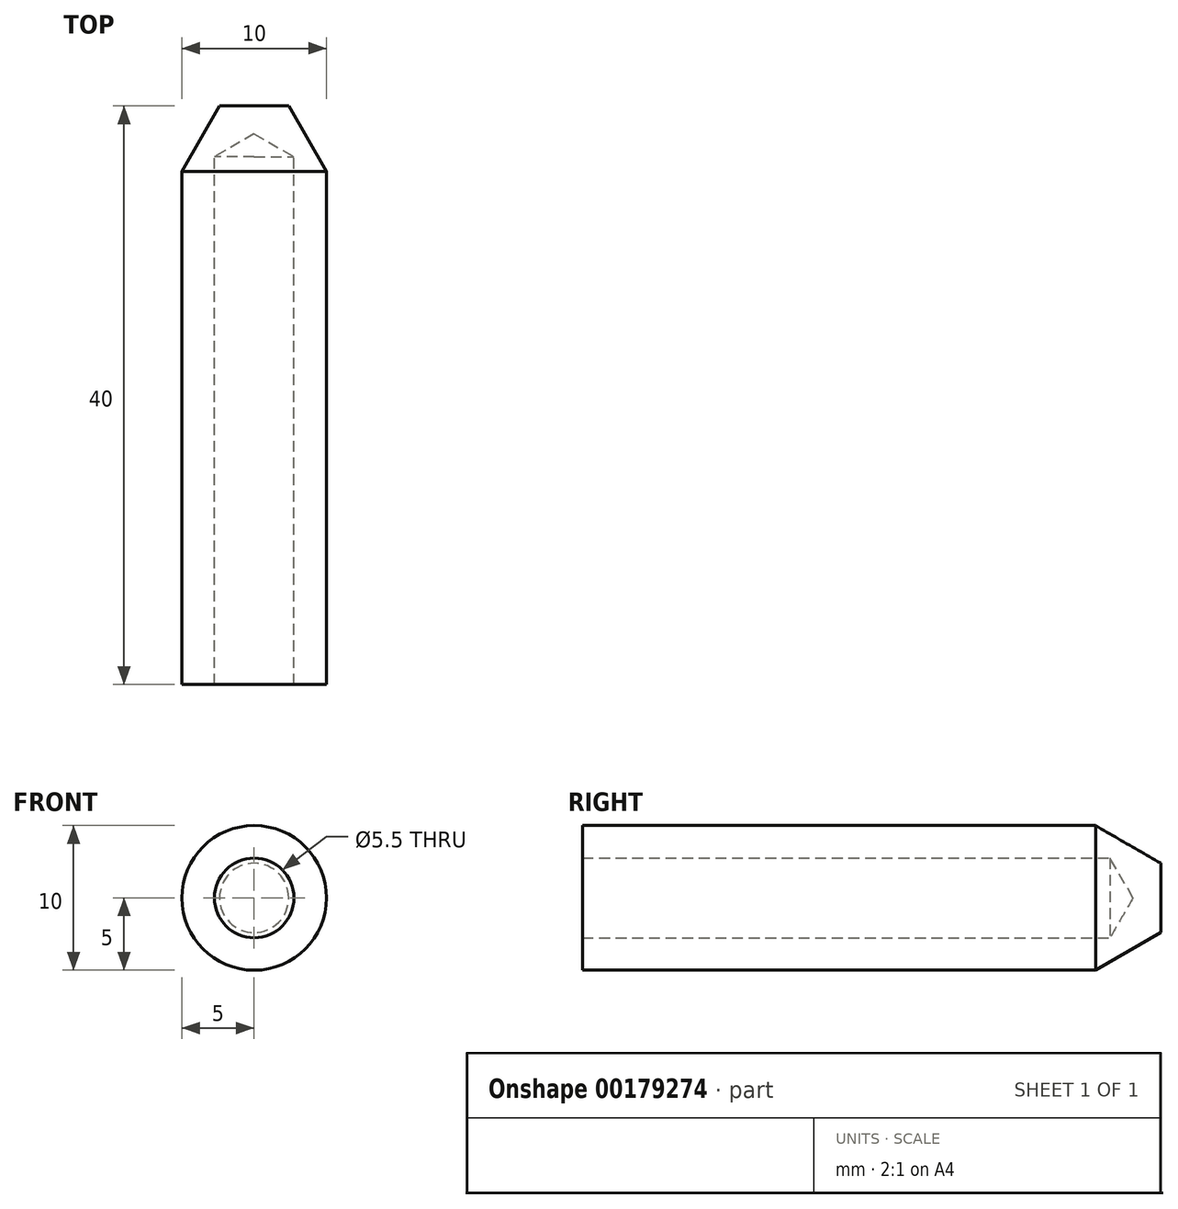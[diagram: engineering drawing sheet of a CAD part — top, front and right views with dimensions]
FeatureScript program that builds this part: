
annotation { "Feature Type Name" : "Feature", "Feature Type Description" : "" }
export const myFeature = defineFeature(function(context is Context, id is Id, definition is map)
    precondition{}
    {
        {
            var Q0;
            Q0=qCreatedBy(makeId("Right.planeOp"),FACE);
            var sketch = newSketch(context, id + "F0", { "sketchPlane" : qUnion([Q0])});
            skLineSegment(sketch, "E0", {"start": v(0, 5) * mm, "end": v(35.49, 5) * mm});
            skLineSegment(sketch, "E1", {"start": v(35.49, 5) * mm, "end": v(40, 2.4) * mm});
            skLineSegment(sketch, "E2", {"start": v(40, 2.4) * mm, "end": v(40, 0) * mm});
            skLineSegment(sketch, "E3", {"start": v(40, 0) * mm, "end": v(38.09, 0) * mm});
            skLineSegment(sketch, "E4", {"start": v(38.09, 0) * mm, "end": v(36.5, 2.75) * mm});
            skLineSegment(sketch, "E5", {"start": v(36.5, 2.75) * mm, "end": v(0, 2.75) * mm});
            skLineSegment(sketch, "E6", {"start": v(0, 2.75) * mm, "end": v(0, 5) * mm});
            skLineSegment(sketch, "E7", {"start": v(37.22, 4) * mm, "end": v(36.5, 2.75) * mm});
            skSolve(sketch);
        }
        {
            var Q0;
            {var subQ1=sQuery(id+"F0.wireOp",EDGE,"E0");Q0=makeQuery(id+"F0.imprint","IMPRINT",FACE,{"disambiguationData":[TD([[makeQuery(id+"F0.imprint","IMPRINT",EDGE,{"derivedFrom":subQ1}),-1.0]])]});}
            var Q1;
            {var subQ0=sQuery(id+"F0.wireOp",EDGE,"E2");Q1=makeQuery(id+"F0.imprint","IMPRINT",FACE,{"disambiguationData":[TD([[makeQuery(id+"F0.imprint","IMPRINT",EDGE,{"derivedFrom":subQ0}),-1.0]])]});}
            var Q2;
            Q2=sQuery(id+"F0.wireOp",EDGE,"E3");
            revolve(context, id + "F1", {"entities" : qUnion([Q0, Q1]), "axis" : qUnion([Q2]), "revolveType" : RevolveType.FULL});
        }
    });
